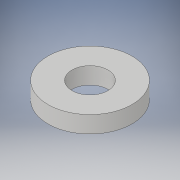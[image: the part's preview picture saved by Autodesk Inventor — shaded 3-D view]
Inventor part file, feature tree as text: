
AUTODESK INVENTOR PART (.ipt)
format: ipt  version: 2018 (Build 220112000, 112)  size: 95,744 bytes
history: native  units: in
note: dims shown in document units (in); Inventor stores cm internally (conversion verified against a paired STEP export)
features: extrude x1, sketch x1
ambient origin geometry x8: Origin, YZ Plane, XZ Plane, XY Plane, X Axis, Y Axis, Z Axis, Center Point
bodies: Solid1 (feature_tree)
feature tree (2):
  extrude  "Extrusion1"  Depth=0.1in
  sketch  "Sketch1"  dims[d0=0.214in d1=0.5in d2=0.1in d3=0.0in]
